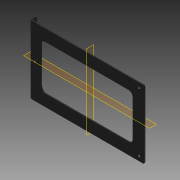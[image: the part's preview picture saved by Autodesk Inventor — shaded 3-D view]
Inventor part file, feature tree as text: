
AUTODESK INVENTOR PART (.ipt)
format: ipt  version: 2015 (Build 190159000, 159)  size: 178,688 bytes
history: native  units: mm
features: extrude x3, fillet x1, hole x1, other x1
ambient origin geometry x8: Origin, YZ Plane, XZ Plane, XY Plane, X Axis, Y Axis, Z Axis, Center Point
bodies: Solid1 (feature_tree)
feature tree (6):
  extrude  "Extrusión1"  Depth=2.0mm
  extrude  "Extrusión2"  Depth=2.0mm
  extrude  "Extrusión3"  Depth=12.0mm
  fillet  "Empalme2"  Radius=130.0mm
  hole  "Agujero2"  [1 undecoded]
  other  "Definición1"
note: 1 required parameter value undecoded (feature->parameter linkage not recoverable at this tier; creation-order binding heuristic only, values carry confidence <= 0.55)
